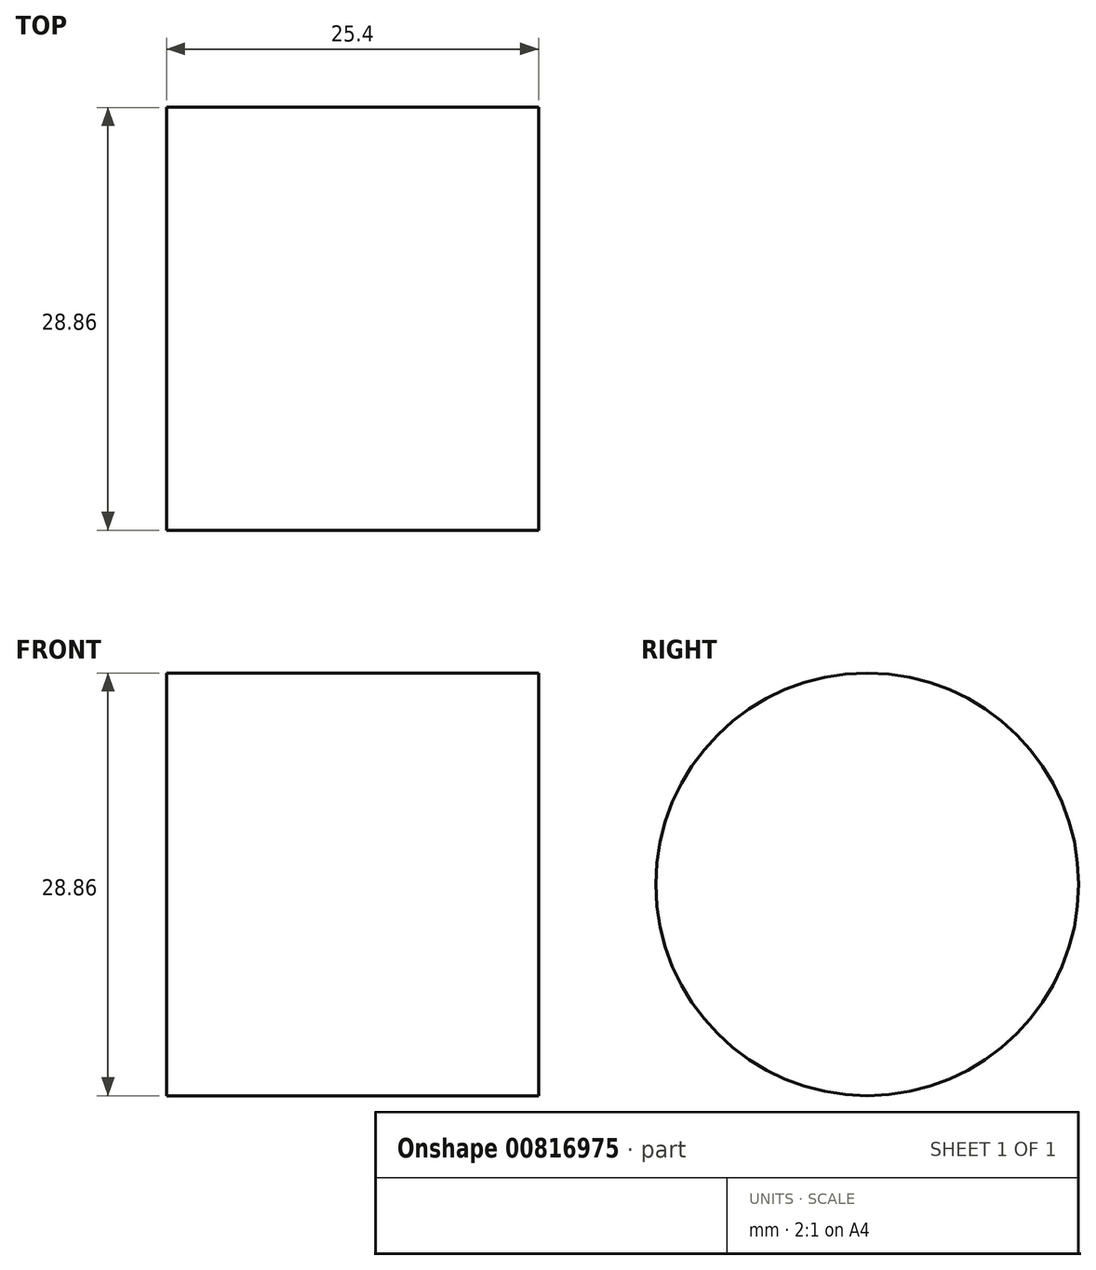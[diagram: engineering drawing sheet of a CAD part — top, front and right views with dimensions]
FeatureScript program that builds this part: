
annotation { "Feature Type Name" : "Feature", "Feature Type Description" : "" }
export const myFeature = defineFeature(function(context is Context, id is Id, definition is map)
    precondition{}
    {
        {
            var Q0;
            Q0=qCreatedBy(makeId("Right.planeOp"),FACE);
            var sketch = newSketch(context, id + "F0", { "sketchPlane" : qUnion([Q0])});
            skCircle(sketch, "E0", {"center": v(-53.8, 35.47) * mm, "radius": 14.43 * mm});
            skSolve(sketch);
        }
        {
            var Q0;
            Q0=sQuery(id+"F0.wireOp",EDGE,"E0");
            extrude(context, id + "F1", {"bodyType" : ToolBodyType.SURFACE, "surfaceEntities" : qUnion([Q0]), "depth" : 25.4 * mm, "offsetDistance" : 25.4 * mm});
        }
    });
